# Revit family: Grohe_ThermostaticShowerMixer_102169KF00
name_source: partatom
category: Plumbing Fixtures
units: mm (PartAtom-declared; Revit-internal decimal feet)

## family parameters
Cut with Voids When Loaded = No
Host = Face
OmniClass Number = 23.45.05.00
OmniClass Title = Sanitary Equipment
Part Type = Normal
Room Calculation Point = No
Round Connector Dimension = Use Diameter
Shared = No

## types (1)
- Thermostatic Shower Mixer (102169KF00)
    Assembly Code = D2013
    AssetType = Fixed
    BIMObjectName = Grohe_ThermostaticShowerMixer_102169KF00
    CO2NeutralProduction = GROHE is one of the first leading manufacturer within the sanitary industry having a CO2-neutral production.
    ClassificationName = Uniclass2015
    ClassificationValue = Pr_40_20_87_75
    Color = Grohe_Black
    Cost = 0 $
    Default Elevation = 0 mm  [stored 0 ft]
    Description = Thermostatic Shower Mixer
    DimensionsDocumentLink = https://cdn.cloud.grohe.com
    DocumentationCertificates = https://www.bimstore.co
    DocumentationInstallationGuide = https://www.bimstore.co
    DocumentationLiterature = https://www.bimstore.co
    DocumentationMaintenance = https://www.bimstore.co
    DocumentationTechnical = https://www.bimstore.co
    DurationUnit = Years
    EF000003 = Wall
    EF000139 = Other
    EF002149 = TRUE
    EF002286 = Insert (push coupling)
    EF002671 = Black
    EF007955 = TRUE
    EF011775 = EB
    EF011779 = TRUE
    EF012753 = 29.00
    EF014578 = true
    EF014591 = false
    EF016731 = Group I,<= 20 dB(A)
    EF020105 = Yes
    EF020259 = Downwards
    EF020780 = Two-grip
    EF020781 = Plastic cartridge
    EF020785 = M26 x 1.5
    EF020787 = Group II, <=30 dB(A)
    EF020788 = false
    EF020791 = Stainless steel
    EF020799 = TRUE
    EF020805 = false
    EF020967 = true
    EF021035 = true
    EF021835 = 150
    EF021855 = false
    EF022042 = Z
    EF022337 = 1/2 inch- 3/4 inch
    EF023686 = Other
    EF023687 = TRUE
    EF023688 = Other
    EF023957 = TRUE
    EF024919 = false
    EF025109 = Other
    EFDE0022 = None
    EFNL0001 = true
    EFSE0002 = true
    Ecojoy = No
    ExpectedLife = 0
    Finish = Black
    FullRecyclabilityOfPlastic = All plastic components are fully recycable
    GROHESocialCommittment = green.grohe.com/social_engagement
    GROHESustainability = green.grohe.com
    IfcExportAs = IfcPipeFitting
    IfcExportType = IfcPipeFittingType
    Keynote = N16
    Manufacturer = Grohe
    ManufacturerName = Grohe
    Model = Thermostatic Shower Mixer
    ModelNumber = 102169KF00
    ModelReference = Thermostatic Shower Mixer
    NBSDescription = Shower fittings package
    NBSObjectName = Grohe - Shower fittings package
    NBSReference = 45-35-70/256
    NominalDepth = 0 mm  [stored 0 ft]
    NominalHeight = 0 mm  [stored 0 ft]
    NominalLength = 0 mm  [stored 0 ft]
    PQDiagramLink = https://cdn.cloud.grohe.com
    PrimaryMaterial = Grohe_Black
    ProductDescription = wall mounted

GROHE CoolTouch no risk of scalding

GROHE Long-Life finish

GROHE SafeStop safety button at 38°C

GROHE SafeStop Plus optional temperature limiter at 43°C included

GROHE TurboStat compact cartridge with wax thermoelement

GROHE ProGrip with knurl structure

GROHE SmartControl push for ON-OFF, turn for volume adjustment from GROHE Water Saving to Full Flow

integrated GROHE EasyReach shower tray

shower bottom outlet 1/2"

built-in non return valves and dirt strainers

protected against backflow
    ProductNumber = 102169KF00
    ProductShortText = Thermostatic shower mixer 1/2"
    ProductType = Thermostat
    ProductionYear = 2023
    SustainabilityAward = green.grohe.com/awards
    SustainabilityReport = green.grohe.com/reporting
    TPIDocumentLink = https://cdn.cloud.grohe.com
    Type Comments = Thermostatic Shower Mixer
    TypeName = Thermostatic Shower Mixer
    URL = https://www.grohe.co.uk
    WarrantyDurationLabor = 0
    WarrantyDurationParts = 0
    WarrantyDurationUnit = Years
    _BSBibleVersion = 17
    _BimSpecGuid = 0
    _CurrentRevision = 1
    _DistributedBy = https://www.bimstore.co
    _ObjectUserGuide = https://www.bimstore.co

note: [stored X ft] marks values corroborated as IEEE doubles in the binary element streams (Revit-internal decimal feet)

## geometry (parser evidence)
native form markers: Sweep x1
no freeform markers — native parametric forms only
